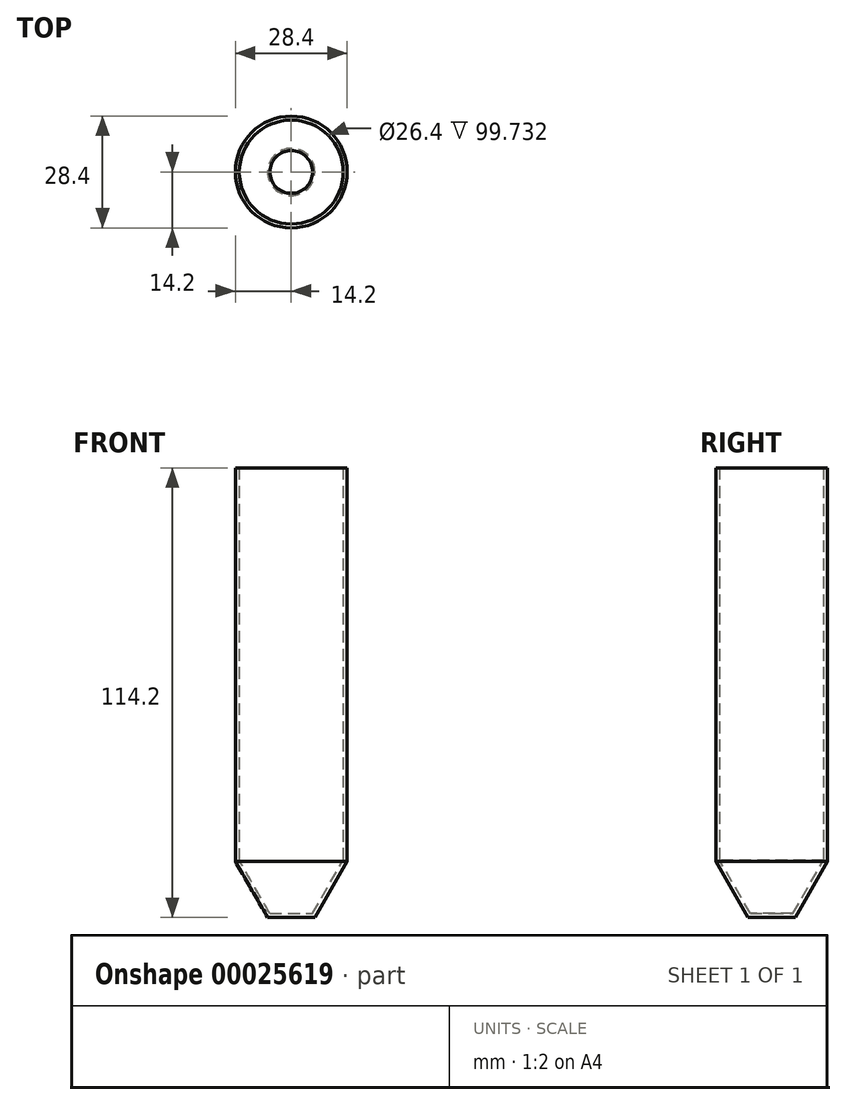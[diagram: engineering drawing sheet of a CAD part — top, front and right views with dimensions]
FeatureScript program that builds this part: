
annotation { "Feature Type Name" : "Feature", "Feature Type Description" : "" }
export const myFeature = defineFeature(function(context is Context, id is Id, definition is map)
    precondition{}
    {
        {
            var Q0;
            Q0=qCreatedBy(makeId("Front.planeOp"),FACE);
            var sketch = newSketch(context, id + "F0", { "sketchPlane" : qUnion([Q0])});
            skLineSegment(sketch, "E0", {"start": v(14.2, 57.55) * mm, "end": v(14.2, -42.45) * mm});
            skLineSegment(sketch, "E1", {"start": v(14.2, -42.45) * mm, "end": v(6, -56.65) * mm});
            skLineSegment(sketch, "E2", {"start": v(6, -56.65) * mm, "end": v(0, -56.65) * mm});
            skLineSegment(sketch, "E3.0", {"start": v(5.42, -55.65) * mm, "end": v(0, -55.65) * mm});
            skLineSegment(sketch, "E3.1", {"start": v(13.2, -42.18) * mm, "end": v(5.42, -55.65) * mm});
            skLineSegment(sketch, "E3.2", {"start": v(13.2, 57.55) * mm, "end": v(13.2, -42.18) * mm});
            skLineSegment(sketch, "E4", {"start": v(13.2, 57.55) * mm, "end": v(14.2, 57.55) * mm});
            skLineSegment(sketch, "E5", {"start": v(0, -56.65) * mm, "end": v(0, -55.65) * mm});
            skLineSegment(sketch, "E6", {"start": v(0, -56.65) * mm, "end": v(0, 57.55) * mm, "construction": true});
            skSolve(sketch);
        }
        {
            var Q0;
            Q0 = qSketchRegion(id + "F0", true);
            var Q1;
            Q1=sQuery(id+"F0.wireOp",EDGE,"E6");
            revolve(context, id + "F1", {"entities" : qUnion([Q0]), "axis" : qUnion([Q1]), "revolveType" : RevolveType.FULL});
        }
    });
